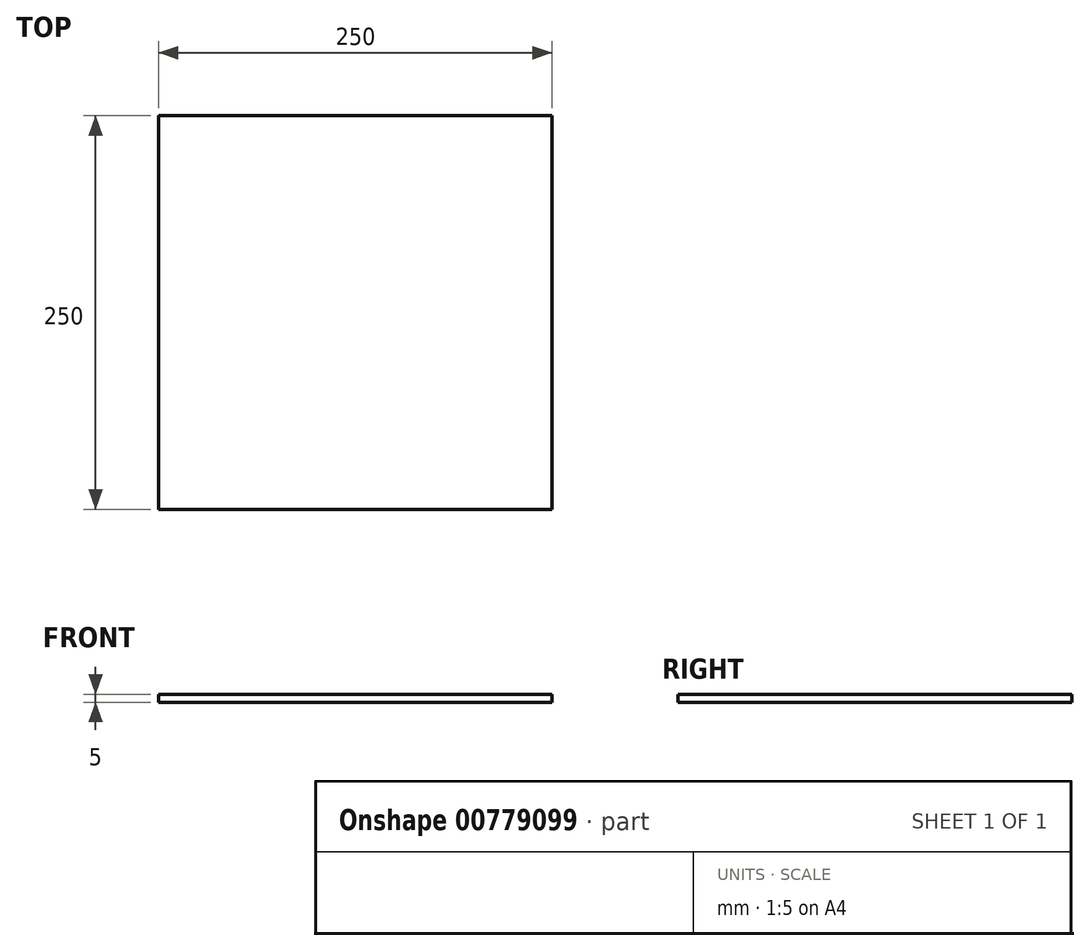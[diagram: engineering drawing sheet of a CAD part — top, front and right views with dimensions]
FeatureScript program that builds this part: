
annotation { "Feature Type Name" : "Feature", "Feature Type Description" : "" }
export const myFeature = defineFeature(function(context is Context, id is Id, definition is map)
    precondition{}
    {
        {
            var Q0;
            Q0=qCreatedBy(makeId("Top.planeOp"),FACE);
            var sketch = newSketch(context, id + "F0", { "sketchPlane" : qUnion([Q0])});
            skLineSegment(sketch, "E0.bottom", {"start": v(0, 0) * mm, "end": v(250, 0) * mm});
            skLineSegment(sketch, "E0.top", {"start": v(0, 250) * mm, "end": v(250, 250) * mm});
            skLineSegment(sketch, "E0.left", {"start": v(0, 0) * mm, "end": v(0, 250) * mm});
            skLineSegment(sketch, "E0.right", {"start": v(250, 0) * mm, "end": v(250, 250) * mm});
            skSolve(sketch);
        }
        {
            var Q0;
            Q0 = qSketchRegion(id + "F0", true);
            extrude(context, id + "F1", {"entities" : qUnion([Q0]), "depth" : 5 * mm, "offsetDistance" : 25 * mm});
        }
    });
